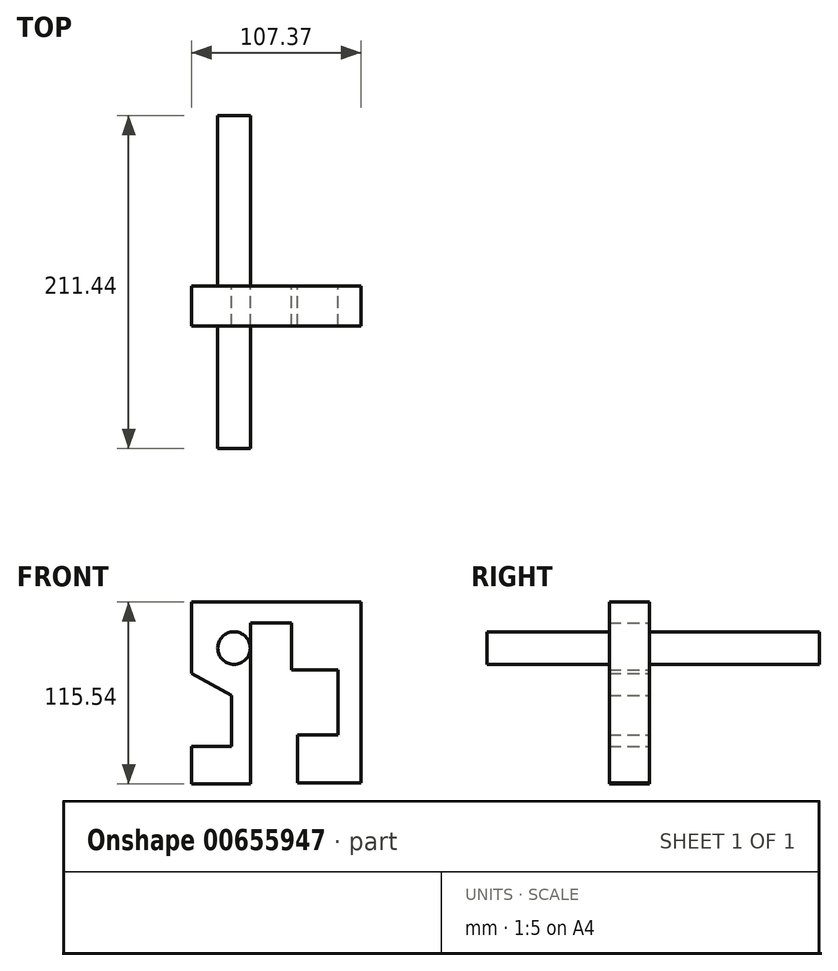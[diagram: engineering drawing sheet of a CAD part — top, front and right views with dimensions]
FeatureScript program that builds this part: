
annotation { "Feature Type Name" : "Feature", "Feature Type Description" : "" }
export const myFeature = defineFeature(function(context is Context, id is Id, definition is map)
    precondition{}
    {
        {
            var Q0;
            Q0=qCreatedBy(makeId("Front.planeOp"),FACE);
            var sketch = newSketch(context, id + "F0", { "sketchPlane" : qUnion([Q0])});
            skLineSegment(sketch, "E0", {"start": v(-54.86, 0) * mm, "end": v(-54.86, 59.19) * mm});
            skLineSegment(sketch, "E1", {"start": v(-54.86, 59.19) * mm, "end": v(52.5, 59.19) * mm});
            skLineSegment(sketch, "E2", {"start": v(52.5, 59.19) * mm, "end": v(52.5, -55.76) * mm});
            skLineSegment(sketch, "E3", {"start": v(52.5, -55.76) * mm, "end": v(12.45, -55.76) * mm});
            skLineSegment(sketch, "E4", {"start": v(12.45, -55.76) * mm, "end": v(12.45, -25.08) * mm});
            skLineSegment(sketch, "E5", {"start": v(12.45, -25.08) * mm, "end": v(38.08, -25.08) * mm});
            skLineSegment(sketch, "E6", {"start": v(38.08, -25.08) * mm, "end": v(38.08, 16.12) * mm});
            skLineSegment(sketch, "E7", {"start": v(38.08, 16.12) * mm, "end": v(8.52, 16.12) * mm});
            skLineSegment(sketch, "E8", {"start": v(8.52, 16.12) * mm, "end": v(8.52, 45.92) * mm});
            skLineSegment(sketch, "E9", {"start": v(8.52, 45.92) * mm, "end": v(-17.45, 45.92) * mm});
            skLineSegment(sketch, "E10", {"start": v(-17.45, 45.92) * mm, "end": v(-17.45, -56.35) * mm});
            skLineSegment(sketch, "E11", {"start": v(-17.45, -56.35) * mm, "end": v(-54.86, -56.35) * mm});
            skLineSegment(sketch, "E12", {"start": v(-54.86, -56.35) * mm, "end": v(-54.86, -32.69) * mm});
            skLineSegment(sketch, "E13", {"start": v(-54.86, -32.69) * mm, "end": v(-29.61, -32.69) * mm});
            skLineSegment(sketch, "E14", {"start": v(-29.61, -32.69) * mm, "end": v(-29.61, 0) * mm});
            skLineSegment(sketch, "E15", {"start": v(-29.61, 0) * mm, "end": v(-54.86, 13.92) * mm});
            skSolve(sketch);
        }
        {
            var Q0;
            {var subQ0=sQuery(id+"F0.wireOp",EDGE,"E1");Q0=makeQuery(id+"F0.imprint","IMPRINT",FACE,{"disambiguationData":[TD([[makeQuery(id+"F0.imprint","IMPRINT",EDGE,{"derivedFrom":subQ0}),-1.0]])]});}
            extrude(context, id + "F1", {"entities" : qUnion([Q0]), "depth" : 25.4 * mm, "offsetDistance" : 25.4 * mm});
        }
        {
            var Q0;
            Q0=qCreatedBy(makeId("Front.planeOp"),FACE);
            var sketch = newSketch(context, id + "F2", { "sketchPlane" : qUnion([Q0])});
            skCircle(sketch, "E16", {"center": v(-28.02, 29.92) * mm, "radius": 10.36 * mm});
            skSolve(sketch);
        }
        {
            var Q0;
            Q0 = qSketchRegion(id + "F2", true);
            extrude(context, id + "F3", {"entities" : qUnion([Q0]), "operationType" : NewBodyOperationType.ADD, "oppositeDirection" : true, "depth" : 82.76 * mm, "offsetDistance" : 25.4 * mm, "hasSecondDirection" : true, "secondDirectionOppositeDirection" : false, "secondDirectionDepth" : 25.4 * mm});
        }
        {
            var Q0;
            Q0=makeQuery(id+"F3.opExtrude","CAP_FACE",FACE,{"disambiguationData":[OSD([sQuery(id+"F2.wireOp",EDGE,"E16")])],"isStart":false});
            extrude(context, id + "F4", {"entities" : qUnion([Q0]), "operationType" : NewBodyOperationType.ADD, "depth" : 25.4 * mm, "offsetDistance" : 25.4 * mm});
        }
        {
            var Q0;
            Q0=makeQuery(id+"F4.opExtrude","CAP_FACE",FACE,{"disambiguationData":[OSD([sQuery(id+"F2.wireOp",EDGE,"E16")])],"isStart":false});
            extrude(context, id + "F5", {"entities" : qUnion([Q0]), "operationType" : NewBodyOperationType.ADD, "oppositeDirection" : true, "depth" : 211.44 * mm, "offsetDistance" : 25.4 * mm});
        }
    });
